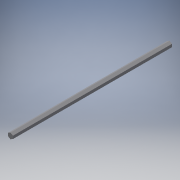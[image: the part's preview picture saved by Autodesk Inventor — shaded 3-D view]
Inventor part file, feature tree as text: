
AUTODESK INVENTOR PART (.ipt)
format: ipt  version: 2016 (Build 200138000, 138)  size: 94,208 bytes
history: native  units: in
note: dims shown in document units (in); Inventor stores cm internally (conversion verified against a paired STEP export)
features: extrude x1, sketch x1
ambient origin geometry x8: Origin, YZ Plane, XZ Plane, XY Plane, X Axis, Y Axis, Z Axis, Center Point
bodies: Solid1 (feature_tree)
feature tree (2):
  extrude  "Extrusion1"  Depth=17.0in TaperAngle=0.0deg
  sketch  "Sketch1"  dims[d0=0.5in d1=17.0in d2=0.0in]
